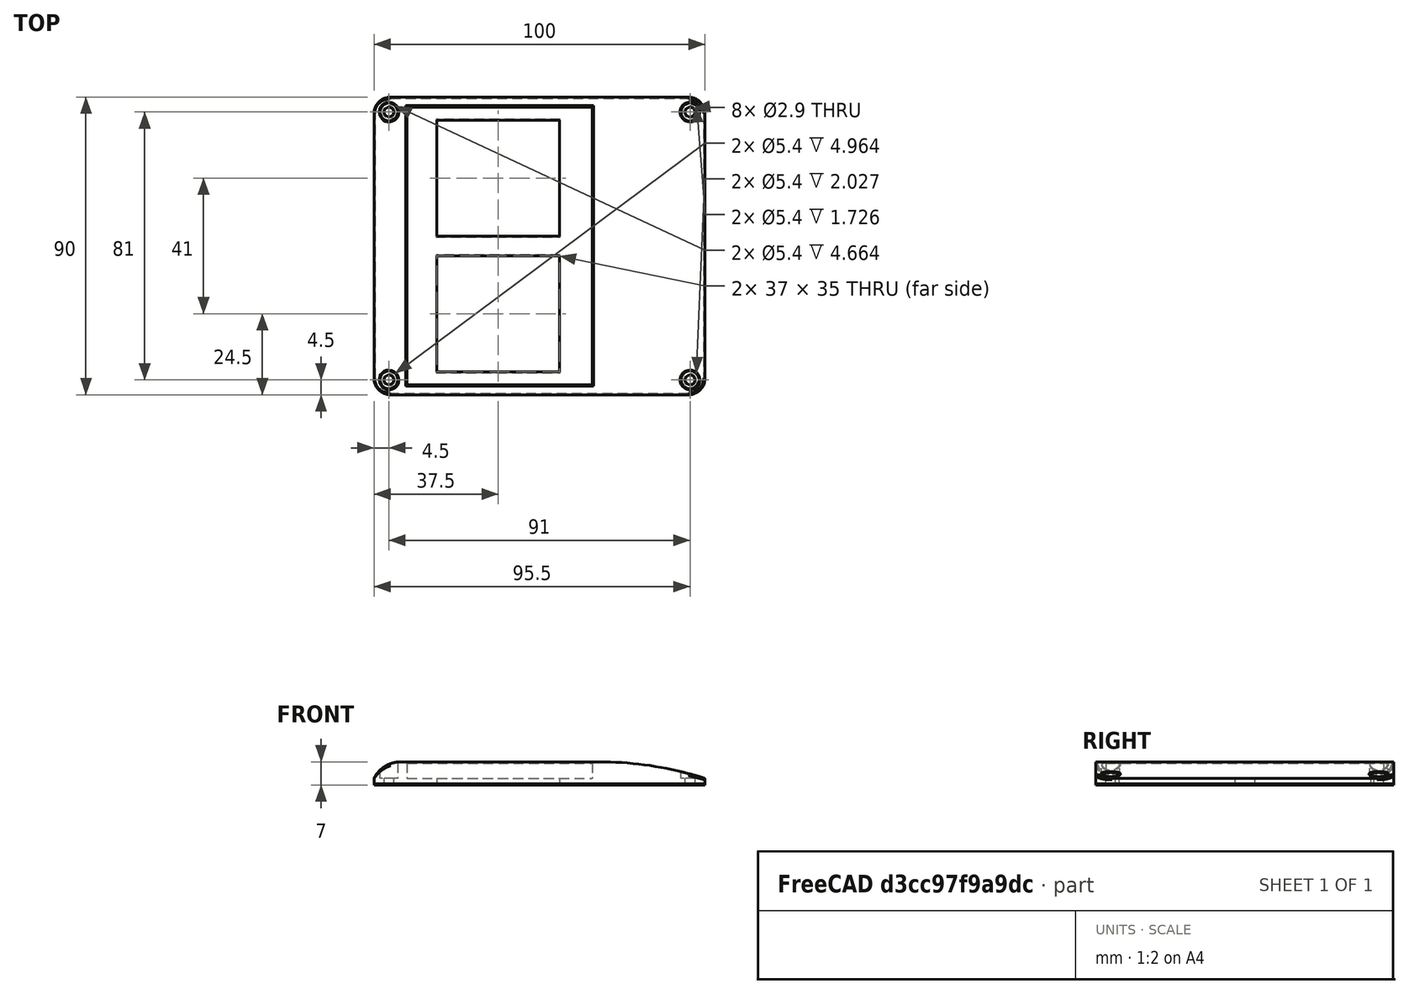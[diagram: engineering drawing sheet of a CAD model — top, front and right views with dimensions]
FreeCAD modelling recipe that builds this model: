
FCSTD DOCUMENT  (FreeCAD 0.18RUnknown)
Label: cover
License: CreativeCommons Attribution
LicenseURL: http://creativecommons.org/licenses/by/4.0/
objects: Sketcher::SketchObject×6, PartDesign::Pocket×5, PartDesign::Chamfer×5, PartDesign::Body×2, Part::Feature×2, PartDesign::Pad×1, PartDesign::FeatureBase×1, PartDesign::Fillet×1, Mesh::Feature×1
note: 29 computed .brp shape members not serialized (recipe doc carries the construction recipe); baked Part::Feature solids carry a one-line shape summary decoded from their .brp

FEATURE [Sketcher::SketchObject] Sketch
  MapMode = 5
  sketch-geometry (8):
    g0: LineSegment StartX=-45 StartY=45 StartZ=0 EndX=45 EndY=45 EndZ=0
    g1: LineSegment StartX=50 StartY=40 StartZ=0 EndX=50 EndY=-40 EndZ=0
    g2: LineSegment StartX=45 StartY=-45 StartZ=0 EndX=-45 EndY=-45 EndZ=0
    g3: LineSegment StartX=-50 StartY=-40 StartZ=0 EndX=-50 EndY=40 EndZ=0
    g4: ArcOfCircle CenterX=-45 CenterY=40 CenterZ=0 NormalX=0 NormalY=0 NormalZ=1 AngleXU=0 Radius=5 StartAngle=1.5708 EndAngle=3.14159
    g5: ArcOfCircle CenterX=45 CenterY=40 CenterZ=0 NormalX=0 NormalY=0 NormalZ=1 AngleXU=0 Radius=5 StartAngle=0 EndAngle=1.5708
    g6: ArcOfCircle CenterX=45 CenterY=-40 CenterZ=0 NormalX=0 NormalY=0 NormalZ=1 AngleXU=0 Radius=5 StartAngle=4.71239 EndAngle=6.28319
    g7: ArcOfCircle CenterX=-45 CenterY=-40 CenterZ=0 NormalX=0 NormalY=0 NormalZ=1 AngleXU=0 Radius=5 StartAngle=3.14159 EndAngle=4.71239
  constraints (18):
    c: Horizontal(g2)
    c: Vertical(g1)
    c: DistanceX(g3,g1) = 100
    c: DistanceY(g2,g0) = 90
    c: Tangent(g0,g4) = 1.5708
    c: Tangent(g0,g5) = 1.5708
    c: Tangent(g1,g5) = 1.5708
    c: Tangent(g3,g4) = 1.5708
    c: Tangent(g2,g7) = 1.5708
    c: Tangent(g7,g3) = 1.5708
    c: Tangent(g2,g6) = 1.5708
    c: Tangent(g1,g6) = 1.5708
    c: Symmetric(g0,g0,g-2)
    c: Equal(g7,g4)
    c: Equal(g4,g5)
    c: Equal(g5,g6)
    c: Radius(g7) = 5
    c: Symmetric(g3,g3,g-1)
FEATURE [PartDesign::Pad] Pad
  Length = 7
  Length2 = 100
  Profile = -> Sketch
  Refine = true
  Type = 0
FEATURE [Sketcher::SketchObject] Sketch005  label="Sketch001"
  MapMode = 5
  Placement = pos=(0,0,7) rot=(0,0,1;0rad)
  Support = -> [Pad]
  sketch-geometry (8):
    g0: Circle CenterX=-45.5 CenterY=40.5 CenterZ=0 NormalX=0 NormalY=0 NormalZ=1 AngleXU=0 Radius=1.45
    g1: Circle CenterX=45.5 CenterY=40.5 CenterZ=0 NormalX=0 NormalY=0 NormalZ=1 AngleXU=0 Radius=1.45
    g2: Circle CenterX=45.5 CenterY=-40.5 CenterZ=0 NormalX=0 NormalY=0 NormalZ=1 AngleXU=0 Radius=1.45
    g3: Circle CenterX=-45.5 CenterY=-40.5 CenterZ=0 NormalX=0 NormalY=0 NormalZ=1 AngleXU=0 Radius=1.45
    g4: LineSegment [constr] StartX=-45.5 StartY=40.5 StartZ=0 EndX=45.5 EndY=40.5 EndZ=0
    g5: LineSegment [constr] StartX=45.5 StartY=40.5 StartZ=0 EndX=45.5 EndY=-40.5 EndZ=0
    g6: LineSegment [constr] StartX=45.5 StartY=-40.5 StartZ=0 EndX=-45.5 EndY=-40.5 EndZ=0
    g7: LineSegment [constr] StartX=-45.5 StartY=-40.5 StartZ=0 EndX=-45.5 EndY=40.5 EndZ=0
  constraints (18):
    c: Equal(g3,g0)
    c: Equal(g0,g1)
    c: Equal(g1,g2)
    c: Coincident(g4,g5)
    c: Coincident(g5,g6)
    c: Coincident(g6,g7)
    c: Coincident(g7,g4)
    c: Horizontal(g4)
    c: Vertical(g7)
    c: Coincident(g4,g0)
    c: Coincident(g5,g2)
    c: Coincident(g4,g1)
    c: Coincident(g6,g3)
    c: Radius(g0) = 1.45
    c: DistanceX(g3,g2) = 91
    c: Symmetric(g3,g2,g-2)
    c: DistanceY(g2,g1) = 81
    c: Symmetric(g1,g2,g-1)
FEATURE [PartDesign::Pocket] Pocket
  BaseFeature = -> Pad
  Length = 5
  Length2 = 100
  Profile = -> Sketch005
  Refine = true
  Type = 1
FEATURE [Sketcher::SketchObject] Sketch007  label="Sketch002"
  MapMode = 5
  Placement = pos=(0,0,7) rot=(0,0,1;0rad)
  Support = -> [Pocket]
  sketch-geometry (10):
    g0: LineSegment StartX=-31 StartY=38 StartZ=0 EndX=6 EndY=38 EndZ=0
    g1: LineSegment StartX=6 StartY=38 StartZ=0 EndX=6 EndY=3 EndZ=0
    g2: LineSegment StartX=6 StartY=3 StartZ=0 EndX=-31 EndY=3 EndZ=0
    g3: LineSegment StartX=-31 StartY=3 StartZ=0 EndX=-31 EndY=38 EndZ=0
    g4: LineSegment StartX=-31 StartY=-3 StartZ=0 EndX=6 EndY=-3 EndZ=0
    g5: LineSegment StartX=6 StartY=-3 StartZ=0 EndX=6 EndY=-38 EndZ=0
    g6: LineSegment StartX=6 StartY=-38 StartZ=0 EndX=-31 EndY=-38 EndZ=0
    g7: LineSegment StartX=-31 StartY=-38 StartZ=0 EndX=-31 EndY=-3 EndZ=0
    g8: LineSegment [constr] StartX=6 StartY=3 StartZ=0 EndX=6 EndY=-3 EndZ=0
    g9: LineSegment [constr] StartX=-31 StartY=-3 StartZ=0 EndX=-31 EndY=3 EndZ=0
  constraints (27):
    c: Coincident(g0,g1)
    c: Coincident(g1,g2)
    c: Coincident(g2,g3)
    c: Coincident(g3,g0)
    c: Horizontal(g0)
    c: Horizontal(g2)
    c: Vertical(g1)
    c: Vertical(g3)
    c: Coincident(g4,g5)
    c: Coincident(g5,g6)
    c: Coincident(g6,g7)
    c: Coincident(g7,g4)
    c: Horizontal(g4)
    c: Horizontal(g6)
    c: Vertical(g5)
    c: Vertical(g7)
    c: Coincident(g8,g1)
    c: Coincident(g8,g4)
    c: Coincident(g9,g4)
    c: Coincident(g9,g2)
    c: Vertical(g9)
    c: Symmetric(g4,g1,g-1)
    c: Equal(g1,g5)
    c: DistanceY(g6,g4) = 35
    c: DistanceX(g0,g0) = 37
    c: DistanceY(g4,g1) = 6
    c: DistanceX(g-1,g1) = 6
FEATURE [PartDesign::Pocket] Pocket001
  BaseFeature = -> Pocket
  Length = 5
  Length2 = 100
  Profile = -> Sketch007
  Refine = true
  Type = 1
FEATURE [Sketcher::SketchObject] Sketch011  label="Sketch003"
  MapMode = 5
  Placement = pos=(0,0,7) rot=(0,0,1;0rad)
  Support = -> [Pocket001]
  sketch-geometry (4):
    g0: LineSegment StartX=-40 StartY=42 StartZ=0 EndX=16 EndY=42 EndZ=0
    g1: LineSegment StartX=16 StartY=42 StartZ=0 EndX=16 EndY=-42 EndZ=0
    g2: LineSegment StartX=16 StartY=-42 StartZ=0 EndX=-40 EndY=-42 EndZ=0
    g3: LineSegment StartX=-40 StartY=-42 StartZ=0 EndX=-40 EndY=42 EndZ=0
  constraints (11):
    c: Coincident(g0,g1)
    c: Coincident(g1,g2)
    c: Coincident(g2,g3)
    c: Coincident(g3,g0)
    c: Horizontal(g0)
    c: Horizontal(g2)
    c: Vertical(g3)
    c: DistanceY(g2,g0) = 84
    c: Symmetric(g1,g0,g-1)
    c: DistanceX(g2,g1) = 56
    c: DistanceX(g-1,g1) = 16
FEATURE [PartDesign::Pocket] Pocket002
  BaseFeature = -> Pocket001
  Length = 5
  Length2 = 100
  Profile = -> Sketch011
  Refine = true
  Type = 0
FEATURE [Sketcher::SketchObject] Sketch009  label="Sketch004"
  MapMode = 5
  Placement = pos=(0,-45,0) rot=(1,0,0;1.5708rad)
  Support = -> [Pocket002]
  sketch-geometry (7):
    g0: LineSegment StartX=-42 StartY=7 StartZ=0 EndX=18 EndY=7 EndZ=0
    g1: ArcOfCircle CenterX=-42 CenterY=-1.9 CenterZ=0 NormalX=0 NormalY=0 NormalZ=1 AngleXU=0 Radius=8.9 StartAngle=1.5708 EndAngle=2.68799
    g2: ArcOfCircle CenterX=18 CenterY=-97.9 CenterZ=0 NormalX=0 NormalY=0 NormalZ=1 AngleXU=0 Radius=104.9 StartAngle=1.2608 EndAngle=1.5708
    g3: LineSegment [constr] StartX=-50 StartY=2 StartZ=0 EndX=50 EndY=2 EndZ=0
    g4: LineSegment StartX=-50 StartY=2 StartZ=0 EndX=-50 EndY=7.1 EndZ=0
    g5: LineSegment StartX=-50 StartY=7.1 StartZ=0 EndX=50 EndY=7.1 EndZ=0
    g6: LineSegment StartX=50 StartY=7.1 StartZ=0 EndX=50 EndY=2 EndZ=0
  constraints (20):
    c: Horizontal(g0)
    c: Coincident(g3,g1)
    c: Coincident(g3,g2)
    c: Horizontal(g3)
    c: DistanceX(g1,g-1) = 50
    c: DistanceX(g-1,g2) = 50
    c: DistanceY(g-1,g1) = 2
    c: DistanceY(g-1,g0) = 7
    c: DistanceX(g0,g0) = 60
    c: DistanceX(g-1,g0) = 18
    c: Tangent(g1,g0) = 1.5708
    c: Tangent(g2,g0) = 1.5708
    c: Coincident(g1,g4)
    c: Coincident(g4,g5)
    c: Horizontal(g5)
    c: Coincident(g5,g6)
    c: Coincident(g6,g2)
    c: Vertical(g6)
    c: DistanceY(g2,g5) = 5.1
    c: Vertical(g4)
FEATURE [PartDesign::Pocket] Pocket003
  BaseFeature = -> Pocket002
  Length = 5
  Length2 = 100
  Profile = -> Sketch009
  Refine = true
  Type = 1
FEATURE [Sketcher::SketchObject] Sketch010  label="Sketch005"
  MapMode = 5
  Placement = pos=(0,1.5e-15,7) rot=(0,0,1;0rad)
  Support = -> [Pocket003]
  sketch-geometry (8):
    g0: Circle CenterX=-45.5 CenterY=40.5 CenterZ=0 NormalX=0 NormalY=0 NormalZ=1 AngleXU=0 Radius=2.7
    g1: Circle CenterX=45.5 CenterY=40.5 CenterZ=0 NormalX=0 NormalY=0 NormalZ=1 AngleXU=0 Radius=2.7
    g2: Circle CenterX=45.5 CenterY=-40.5 CenterZ=0 NormalX=0 NormalY=0 NormalZ=1 AngleXU=0 Radius=2.7
    g3: Circle CenterX=-45.5 CenterY=-40.5 CenterZ=0 NormalX=0 NormalY=0 NormalZ=1 AngleXU=0 Radius=2.7
    g4: LineSegment [constr] StartX=-45.5 StartY=40.5 StartZ=0 EndX=45.5 EndY=40.5 EndZ=0
    g5: LineSegment [constr] StartX=45.5 StartY=40.5 StartZ=0 EndX=45.5 EndY=-40.5 EndZ=0
    g6: LineSegment [constr] StartX=45.5 StartY=-40.5 StartZ=0 EndX=-45.5 EndY=-40.5 EndZ=0
    g7: LineSegment [constr] StartX=-45.5 StartY=-40.5 StartZ=0 EndX=-45.5 EndY=40.5 EndZ=0
  constraints (18):
    c: Equal(g3,g0)
    c: Equal(g0,g1)
    c: Equal(g1,g2)
    c: Coincident(g4,g5)
    c: Coincident(g5,g6)
    c: Coincident(g6,g7)
    c: Coincident(g7,g4)
    c: Horizontal(g4)
    c: Vertical(g7)
    c: Coincident(g4,g0)
    c: Coincident(g5,g2)
    c: Coincident(g4,g1)
    c: Coincident(g6,g3)
    c: Radius(g0) = 2.7
    c: DistanceX(g3,g2) = 91
    c: Symmetric(g3,g2,g-2)
    c: DistanceY(g2,g1) = 81
    c: Symmetric(g1,g2,g-1)
FEATURE [PartDesign::Pocket] Pocket004
  BaseFeature = -> Pocket003
  Length = 5
  Length2 = 100
  Profile = -> Sketch010
  Refine = true
  Type = 0
FEATURE [PartDesign::Body] Body
  Group = -> [Sketch,Pad,Sketch005,Pocket,Sketch007,Pocket001,Sketch009,Sketch010,Sketch011,Pocket002,Pocket003,Pocket004]
  Origin = -> Origin
  Tip = -> Pocket004
FEATURE [Part::Feature] Pocket004001  label="Pocket005"
  shape: bbox 100 x 90 x 7 mm, 37 faces (baked)
FEATURE [PartDesign::FeatureBase] BaseFeature
  BaseFeature = -> Pocket004001
FEATURE [PartDesign::Chamfer] Chamfer
  Base = -> BaseFeature [Edge7,Edge9,Edge11,Edge10,Edge8,Edge6,Edge1,Edge5]
  BaseFeature = -> BaseFeature
  Size = 0.4
FEATURE [PartDesign::Chamfer] Chamfer001
  Base = -> Chamfer [Edge32,Edge41,Edge42,Edge43]
  BaseFeature = -> Chamfer
  Size = 0.4
FEATURE [PartDesign::Chamfer] Chamfer002
  Base = -> Chamfer001 [Edge10,Edge11,Edge12,Edge13,Edge15,Edge14,Edge17,Edge16]
  BaseFeature = -> Chamfer001
  Size = 0.3
FEATURE [PartDesign::Fillet] Fillet
  Base = -> Chamfer002 [Edge74,Edge78,Edge72,Edge75,Edge80,Edge85,Edge88,Edge89,Edge77,Edge86,Edge90,Edge83]
  BaseFeature = -> Chamfer002
  Radius = 0.6
FEATURE [PartDesign::Chamfer] Chamfer003
  Base = -> Fillet [Edge34,Edge35,Edge70,Edge69]
  BaseFeature = -> Fillet
  Size = 0.3
FEATURE [PartDesign::Chamfer] Chamfer004
  Base = -> Chamfer003 [Edge14,Edge15,Edge16,Edge17]
  BaseFeature = -> Chamfer003
  Size = 0.4
FEATURE [PartDesign::Body] Body001
  BaseFeature = -> Pocket004001
  Group = -> [BaseFeature,Chamfer,Chamfer001,Chamfer002,Fillet,Chamfer003,Chamfer004]
  Origin = -> Origin001
  Tip = -> Chamfer004
FEATURE [Part::Feature] Chamfer004001  label="Chamfer005"
  shape: bbox 100 x 90 x 7.906 mm, 77 faces (baked)
FEATURE [Mesh::Feature] Mesh  label="Chamfer005 (Meshed)"
